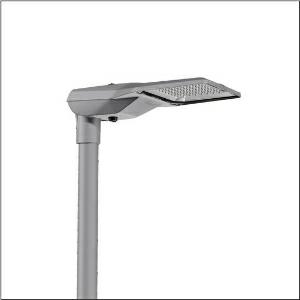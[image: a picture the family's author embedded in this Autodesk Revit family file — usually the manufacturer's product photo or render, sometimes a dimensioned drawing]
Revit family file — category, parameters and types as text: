
# Revit family: streetlight_sl_21_midi___p0_5a_5xe3v33t08nb_a5b7
name_source: partatom
category: Lighting Fixtures
units: mm (PartAtom-declared; Revit-internal decimal feet)

## family parameters
Cut with Voids When Loaded = No
Host = Face
Light Source = No
Part Type = Normal
Room Calculation Point = No
Round Connector Dimension = Use Diameter
Shared = No

## types (1)
- --- (1 x LED, 22310 lm, 151.2 W, 3000K)
    Apparent Load = 151 VA
    CIE Flux Codes = 37 73 96 100 100
    Color Rendering = 70
    Color Temperature = 3000K
    Default Elevation = 1800 mm
    Description = Streetlight SL 21 midi, mast luminaire, primary light control with lens, of PMMA, primary optical cover: cover, of toughened safety glass, transparent, light distribution: P0.5a, light emission: direct distribution, primary light characteristic: asymmetric, installation type: post-top, side-entry, LED, High Power LED, rated luminous flux: 22.310lm, luminous efficacy: 148lm/W, light colour: 730, colour temperature: 3000K, control gear: D4i, control: overheat protection, constant luminous flux control, time-dependent luminous flux control, flexible luminous flux parameterisation, pre-setting: logarithmic dimming characteristic, mains connection: 230..240V, AC, 50/60Hz, start of lifetime: 151W, end of service life: 157W, reduction: 70W, luminaire housing, of diecast aluminium, powder-coated, Siteco® metallic grey (DB 702S), corrosivity category C5 mid according to DIN EN ISO 12944, multi-level sealing system, sealing non-destructively replaceable, inclination adjustable: 0°, 5°, 10°, 15°, please order mast flange separately, length: 644mm, width: 335mm, height: 110mm, mast flange for spigot size: 42mm (side-entry): 5XC10008XM4, 60/48mm (side-entry/post-top): 5XC10108XM2, 76/60mm (side-entry/post-top): 5XC10108XM1, mounting height: 4..8m, Smart Interface below and above, protection rating (complete): IP66, insulation class (complete): insulation class II (safety insulation), certification: CE, ENEC, ENEC+, VDE, impact resistance: IK10, permissible operating ambient temperature for outdoor applications: -40..+50°C, standard-compliant lighting for roads and squares, packaging unit: 1 piece

Light Distribution: P0.5a
    Height = 111 mm
    Lamp = 1 x LED
    Lamp Light Flux = 22310 lm
    Lamp Power = 151.2 W
    Lamp count = 1
    Length = 644 mm
    Luminous efficacy = 148 lm/W
    Manufacturer = Siteco
    ModVariant = No
    Model = 5XE3V33T08NB
    Number of Poles = 1
    OnlyDefault = Yes
    Power Factor = 1
    Product Name = Streetlight SL 21 midi | P0.5a
    Product group = mast luminaire | pylon top
    ProductGroupID = 6100
    Protection Class = Protection class II
    Protection Degree = IP 66
    RLX_Detail_Level = 1
    RLX_Emergency_Light_Flux = 0 lm
    RLX_Emergency_Type = 0
    RLX_Emergency_Type_DB = No
    RlxData = <blob elided: 90337 chars, md5=1c08e3c6>
    Socket = socket
    Standby Power = 0 W
    System Light Flux = 22310 lm
    System Power = 151 W
    Type Comments = factory setting: luminous flux: 100 % | dim-lin: 254 | 802 mA
    Type Image = l_1004304.jpg
    URL = http://relux.com
    VarID = @adj_090527
    Voltage = 0 V
    Weight = 0.00 kg
    Width = 336 mm

## geometry (parser evidence)
native form markers: Blend x4, Sweep x11
no freeform markers — native parametric forms only
